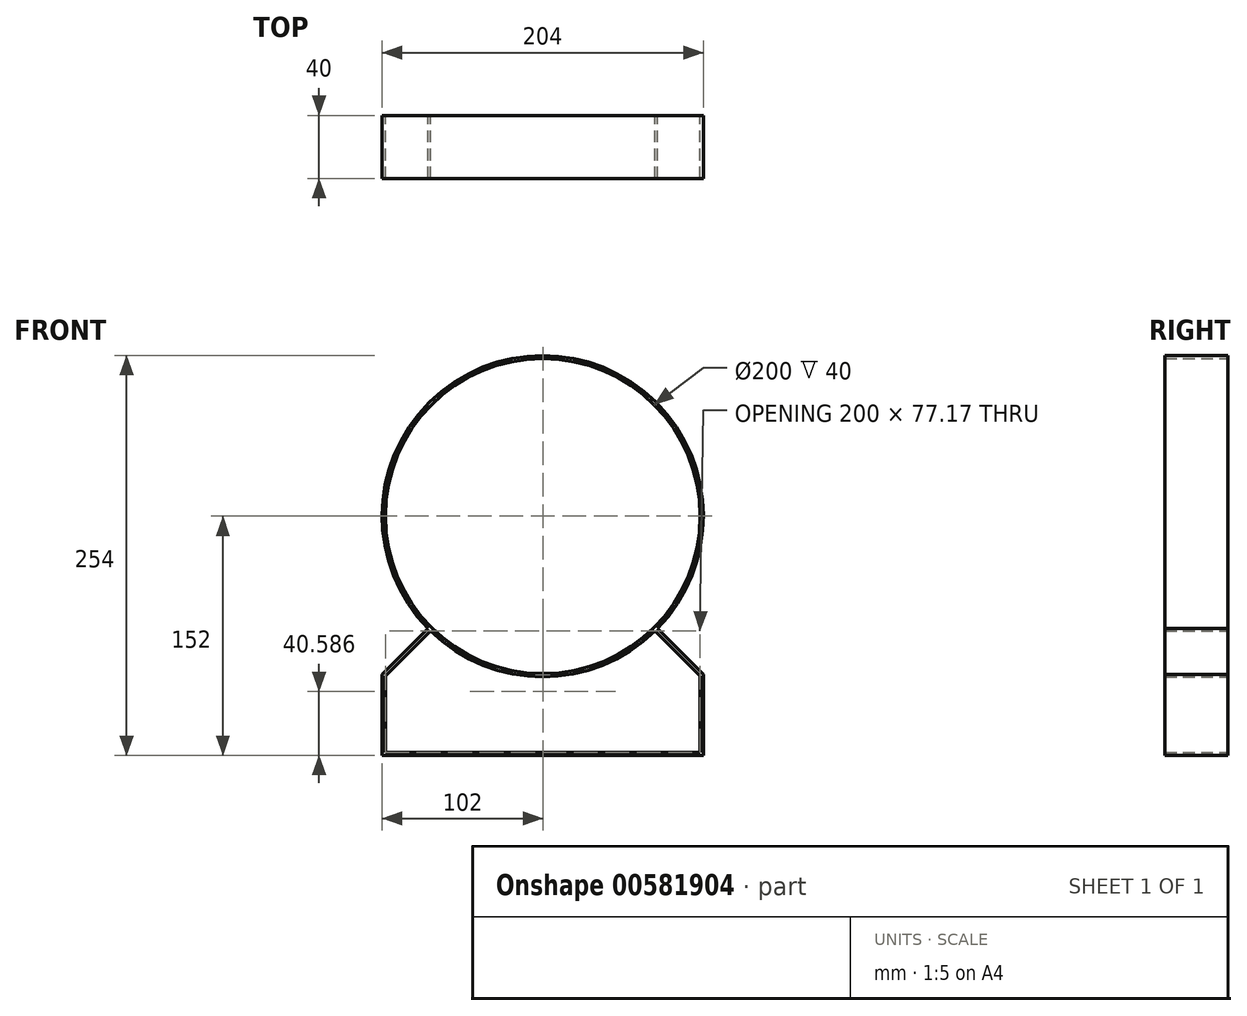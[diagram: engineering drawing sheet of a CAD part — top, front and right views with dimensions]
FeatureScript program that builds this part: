
annotation { "Feature Type Name" : "Feature", "Feature Type Description" : "" }
export const myFeature = defineFeature(function(context is Context, id is Id, definition is map)
    precondition{}
    {
        {
            var Q0;
            Q0=qCreatedBy(makeId("Front.planeOp"),FACE);
            var sketch = newSketch(context, id + "F0", { "sketchPlane" : qUnion([Q0])});
            skLineSegment(sketch, "E0", {"start": v(0, 0) * mm, "end": v(-679.96, 0) * mm, "construction": true});
            skLineSegment(sketch, "E1", {"start": v(0, 0) * mm, "end": v(0, 658.78) * mm, "construction": true});
            skLineSegment(sketch, "E2", {"start": v(0, 0) * mm, "end": v(-291.77, -291.77) * mm, "construction": true});
            skLineSegment(sketch, "E3", {"start": v(0, 0) * mm, "end": v(291.77, -291.77) * mm, "construction": true});
            skCircle(sketch, "E4", {"center": v(0, 0) * mm, "radius": 100 * mm});
            skCircle(sketch, "E5", {"center": v(0, 0) * mm, "radius": 102 * mm});
            skLineSegment(sketch, "E6", {"start": v(-102, -152) * mm, "end": v(0, -152) * mm});
            skLineSegment(sketch, "E7", {"start": v(-100, -150) * mm, "end": v(0, -150) * mm});
            skLineSegment(sketch, "E8", {"start": v(0, 0) * mm, "end": v(0, -311.11) * mm, "construction": true});
            skLineSegment(sketch, "E9", {"start": v(-100, -150) * mm, "end": v(-100, -101.41) * mm});
            skLineSegment(sketch, "E10", {"start": v(-102, -152) * mm, "end": v(-102, -100.59) * mm});
            skLineSegment(sketch, "E11", {"start": v(-72.83, -71.41) * mm, "end": v(-102, -100.59) * mm});
            skLineSegment(sketch, "E12", {"start": v(-71.41, -72.83) * mm, "end": v(-100, -101.41) * mm});
            skLineSegment(sketch, "E13.MirrorCS", {"start": v(71.41, -72.83) * mm, "end": v(100, -101.41) * mm});
            skLineSegment(sketch, "E14.MirrorCS", {"start": v(102, -152) * mm, "end": v(0, -152) * mm});
            skLineSegment(sketch, "E15.MirrorCS", {"start": v(100, -150) * mm, "end": v(0, -150) * mm});
            skLineSegment(sketch, "E16.MirrorCS", {"start": v(72.83, -71.41) * mm, "end": v(102, -100.59) * mm});
            skLineSegment(sketch, "E17.MirrorCS", {"start": v(100, -150) * mm, "end": v(100, -101.41) * mm});
            skLineSegment(sketch, "E18.MirrorCS", {"start": v(102, -152) * mm, "end": v(102, -100.59) * mm});
            skSolve(sketch);
        }
        {
            var Q0;
            Q0=qSketchRegion(id+"F0",true);
            extrude(context, id + "F1", {"entities" : qUnion([Q0]), "offsetDistance" : 25 * mm, "depth" : 40 * mm});
        }
    });
